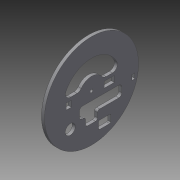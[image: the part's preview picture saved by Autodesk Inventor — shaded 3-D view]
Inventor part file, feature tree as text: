
AUTODESK INVENTOR PART (.ipt)
format: ipt  version: 2016 (Build 200138000, 138)  size: 202,240 bytes
history: native  units: mm
features: extrude x6, sketch x5, fillet x2
ambient origin geometry x8: Origin, YZ Plane, XZ Plane, XY Plane, X Axis, Y Axis, Z Axis, Center Point
bodies: Body1 (feature_tree)
feature tree (13):
  extrude  "Extrusion3"  Depth=28.0mm
  extrude  "Extrusion5"  Depth=3.0mm
  extrude  "Extrusion6"  Depth=3.0mm TaperAngle=0.0deg
  extrude  "Extrusion9"  Depth=5.0mm
  fillet  "Fillet1"  Radius=3.0mm
  extrude  "Extrusion10"  Depth=10.0mm
  fillet  "Fillet2"  Radius=10.0mm
  extrude  "Extrusion11"  Depth=12.5mm
  sketch  "Sketch2"  dims[d0=94.0mm d5=28.0mm]
  sketch  "Sketch4"  dims[d6=25.0mm d7=3.0mm]
  sketch  "Sketch7"  dims[d8=47.0mm d36=3.0mm d37=0.0mm]
  sketch  "Sketch8"  dims[d53=5.0mm d54=5.0mm d55=3.0mm d56=0.0mm]
  sketch  "Sketch9"  dims[d59=5.0mm d60=20.0mm d62=10.0mm d63=12.5mm d64=3.0mm d65=0.0mm d86=12.0mm d90=8.5mm d91=3.0mm d94=6.0mm d95=93.0mm d96=3.0mm d97=42.0mm d98=11.0mm d99=5.0mm d100=3.0mm d101=40.0mm d102=6.0mm d104=2.0mm d105=12.0mm d106=8.5mm d107=10.0mm d108=0.0mm d109=2.0mm d110=12.0mm d111=8.0mm d112=29.0mm d113=7.0mm d114=10.0mm d115=0.0mm d116=1.0mm d117=10.0mm d118=22.5mm d119=21.0mm d120=10.0mm d121=0.0mm]
